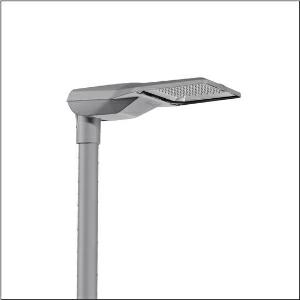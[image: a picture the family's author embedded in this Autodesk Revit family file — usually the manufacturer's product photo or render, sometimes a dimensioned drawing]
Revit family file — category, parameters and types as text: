
# Revit family: streetlight_sl_21_iq_midi___st0_8a_5xe3c41d08nb_52df
name_source: partatom
category: Lighting Fixtures
units: mm (PartAtom-declared; Revit-internal decimal feet)

## family parameters
Cut with Voids When Loaded = No
Host = Face
Light Source = No
Part Type = Normal
Room Calculation Point = No
Round Connector Dimension = Use Diameter
Shared = No

## types (1)
- --- (1 x LED, 24250 lm, 155.5 W, 4000K)
    Apparent Load = 155 VA
    CIE Flux Codes = 41 75 97 100 100
    Color Rendering = 70
    Color Temperature = 4000K
    Default Elevation = 1800 mm
    Description = Streetlight SL 21 iQ midi, mast luminaire, primary light control with lens, of PMMA, primary optical cover: cover, of toughened safety glass, transparent, light distribution: ST0.8a, light emission: direct distribution, primary light characteristic: asymmetric, installation type: post-top, side-entry, LED, High Power LED, rated luminous flux: 24.250lm, luminous efficacy: 156lm/W, light colour: 740, colour temperature: 4000K, control: Auto-Match, Temp-Guard, Lumen-Switch, Night-Set, Smart-Wire, Light-Fading, Desk-Remote (wireless, voltage-free reading and setting of iQ features in the workshop via application-optimized NFC function/RFID function), optimised constant luminous flux control (CLO 2.0), presetting dimming linear, mains connection: 230..240V, AC, 50/60Hz, start of lifetime: 156W, end of service life: 162W, reduction: 69W, luminaire housing, of diecast aluminium, powder-coated, Siteco® metallic grey (DB 702S), corrosivity category C5 mid according to DIN EN ISO 12944, please order mast flange separately, inclination adjustable: 0°, 5°, 10°, 15°, sealing non-destructively replaceable, multi-level sealing system, length: 644mm, width: 335mm, height: 110mm, mast flange for spigot size: 42mm (side-entry): 5XC10008XM4, 60/48mm (side-entry/post-top): 5XC10108XM2, 76/60mm (side-entry/post-top): 5XC10108XM1, protection rating (complete): IP66, insulation class (complete): insulation class II (safety insulation), certification: CE, ENEC, ENEC+, VDE, impact resistance: IK09, permissible operating ambient temperature for outdoor applications: -40..+50°C, standard-compliant lighting for roads and squares, packaging unit: 1 piece

Light Distribution: ST0.8a
    Height = 111 mm
    Lamp = 1 x LED
    Lamp Light Flux = 24250 lm
    Lamp Power = 155.5 W
    Lamp count = 1
    Length = 644 mm
    Luminous efficacy = 156 lm/W
    Manufacturer = Siteco
    ModVariant = No
    Model = 5XE3C41D08NB
    Number of Poles = 1
    OnlyDefault = Yes
    Power Factor = 1
    Product Name = Streetlight SL 21 iQ midi | ST0.8a
    Product group = mast luminaire | pylon top
    ProductGroupID = 6100
    Protection Class = Protection class II
    Protection Degree = IP 66
    RLX_Detail_Level = 1
    RLX_Emergency_Light_Flux = 0 lm
    RLX_Emergency_Type = 0
    RLX_Emergency_Type_DB = No
    RlxData = <blob elided: 90841 chars, md5=3070d4aa>
    Socket = socket
    Standby Power = 0 W
    System Light Flux = 24250 lm
    System Power = 155 W
    Type Comments = factory setting: luminous flux: 100 % | dim-lin: 254 | 823 mA
    Type Image = l_1004298.jpg
    URL = http://relux.com
    VarID = @adj_101345
    Voltage = 0 V
    Weight = 0.00 kg
    Width = 336 mm

## geometry (parser evidence)
native form markers: Blend x4, Sweep x11
no freeform markers — native parametric forms only
